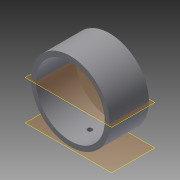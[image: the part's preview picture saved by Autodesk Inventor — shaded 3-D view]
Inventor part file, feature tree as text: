
AUTODESK INVENTOR PART (.ipt)
format: ipt  version: 2014 (Build 180170000, 170)  size: 94,720 bytes
history: native  units: in
note: dims shown in document units (in); Inventor stores cm internally (conversion verified against a paired STEP export)
features: extrude x2, sketch x2, plane x1
ambient origin geometry x8: Origin, YZ Plane, XZ Plane, XY Plane, X Axis, Y Axis, Z Axis, Center Point
bodies: Solid1 (feature_tree)
feature tree (5):
  extrude  "Extrusion1"  Depth=0.125in
  plane  "Work Plane1"
  extrude  "Extrusion2"  Depth=1.0in
  sketch  "Sketch1"  dims[d2=2.0in d3=0.125in]
  sketch  "Sketch2"  dims[d4=1.0in d5=0.0in d6=0.125in d7=0.5in d8=1.0in d9=0.0in]
